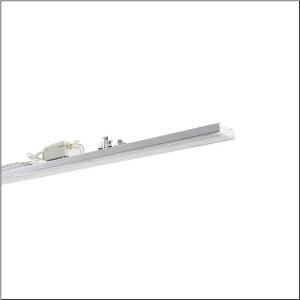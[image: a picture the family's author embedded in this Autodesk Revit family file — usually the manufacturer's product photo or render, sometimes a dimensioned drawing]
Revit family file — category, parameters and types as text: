
# Revit family: licross_r__11_recessed_mo_51tl12cn44xg_a92d
name_source: partatom
category: Lighting Fixtures
units: mm (PartAtom-declared; Revit-internal decimal feet)

## family parameters
Cut with Voids When Loaded = No
Host = Face
Light Source = No
Part Type = Normal
Room Calculation Point = No
Round Connector Dimension = Use Diameter
Shared = No

## types (1)
- Licross® 11 Recessed MO (1 x LED, 4300 lm, 21.9 W, 4000K)
    Apparent Load = 22 VA
    CIE Flux Codes = 67 92 99 100 100
    Color Rendering = 80
    Color Temperature = 4000K
    Default Elevation = 1800 mm
    Description = Licross® 11 Recessed MO, luminaire insert, of sheet steel, coil coated, white, length: 1.500mm, width: 66mm, height: 67mm, LED rated luminous flux: 4.300lm, light colour: 840, control gear: ON/OFF, CLOi, with plug, 3-pole, with phase selection, mains connection: 220..240V, AC, 50/60Hz, start of lifetime: 22W, end of service life: 24W, halogen-free wiring, primary optical cover: cover, of PMMA, light emission: direct distribution, primary light characteristic: symmetric, protection rating (complete): IP40, insulation class (complete): insulation class I (protective earthing), certification: CE, ENEC, VDE, UKCA, protection symbol: D if used in an environment without relevant dust loads with corresponding accessories, impact resistance: IK06, permissible ambient temperature for indoor applications: -35..+50°C, corresponds to IFS (International Featured Standards) requirements for safety and quality in the food industry, reducing of maximum allowable ambient temperature of 5°C with ceiling mounting, LABS conformity tested according to VDMA 24364:2018-05, packaging unit: 1 piece
    Height = 58 mm
    Lamp = 1 x LED
    Lamp Light Flux = 4300 lm
    Lamp Power = 21.9 W
    Lamp count = 1
    Length = 1500 mm
    Luminous efficacy = 196 lm/W
    Manufacturer = Siteco
    ModVariant = No
    Model = 51TL12CN44XG
    Mounting Place = Ceiling
    Mounting Type = Pendant
    Number of Poles = 1
    OnlyDefault = Yes
    Power Factor = 1
    Product Name = Licross® 11 Recessed MO
    Product group = luminaire insert
    ProductGroupID = 901
    Protection Class = Protection class I
    Protection Degree = IP 40
    RLX_Detail_Level = 1
    RLX_Emergency_Light_Flux = 0 lm
    RLX_Emergency_Type = 0
    RLX_Emergency_Type_DB = No
    RlxData = <blob elided: 20829 chars, md5=3b7b9abf>
    Socket = socket
    Standby Power = 0 W
    System Light Flux = 4300 lm
    System Power = 22 W
    Type Comments = Product without accessories
    Type Image = l_1296930.jpg
    URL = http://relux.com
    VarID = ---
    Voltage = 0 V
    Weight = 0.00 kg
    Width = 66 mm

## geometry (parser evidence)
native form markers: Blend x4, Sweep x11
no freeform markers — native parametric forms only
